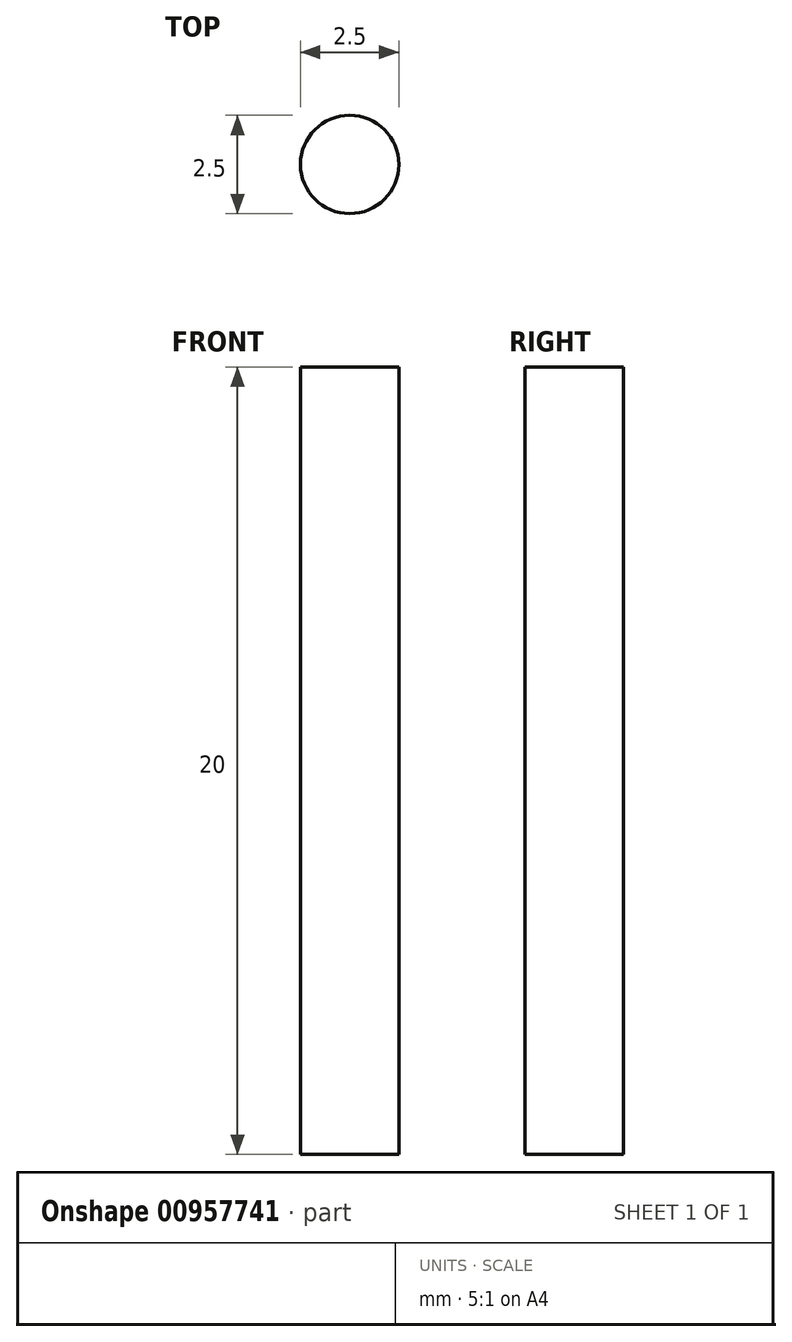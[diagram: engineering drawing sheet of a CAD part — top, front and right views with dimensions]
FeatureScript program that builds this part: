
annotation { "Feature Type Name" : "Feature", "Feature Type Description" : "" }
export const myFeature = defineFeature(function(context is Context, id is Id, definition is map)
    precondition{}
    {
        {
            var Q0;
            Q0=qCreatedBy(makeId("Top.planeOp"),FACE);
            var sketch = newSketch(context, id + "F0", { "sketchPlane" : qUnion([Q0])});
            skCircle(sketch, "E0", {"center": v(0, 0) * mm, "radius": 1.25 * mm});
            skSolve(sketch);
        }
        {
            var Q0;
            Q0=makeQuery(id+"F0.imprint","IMPRINT",FACE,{"disambiguationData":[TD([[makeQuery(id+"F0.imprint","IMPRINT",EDGE,{"derivedFrom":sQuery(id+"F0.wireOp",EDGE,"E0")}),1.0]])]});
            extrude(context, id + "F1", {"entities" : qUnion([Q0]), "depth" : 20 * mm, "offsetDistance" : 25 * mm});
        }
    });
